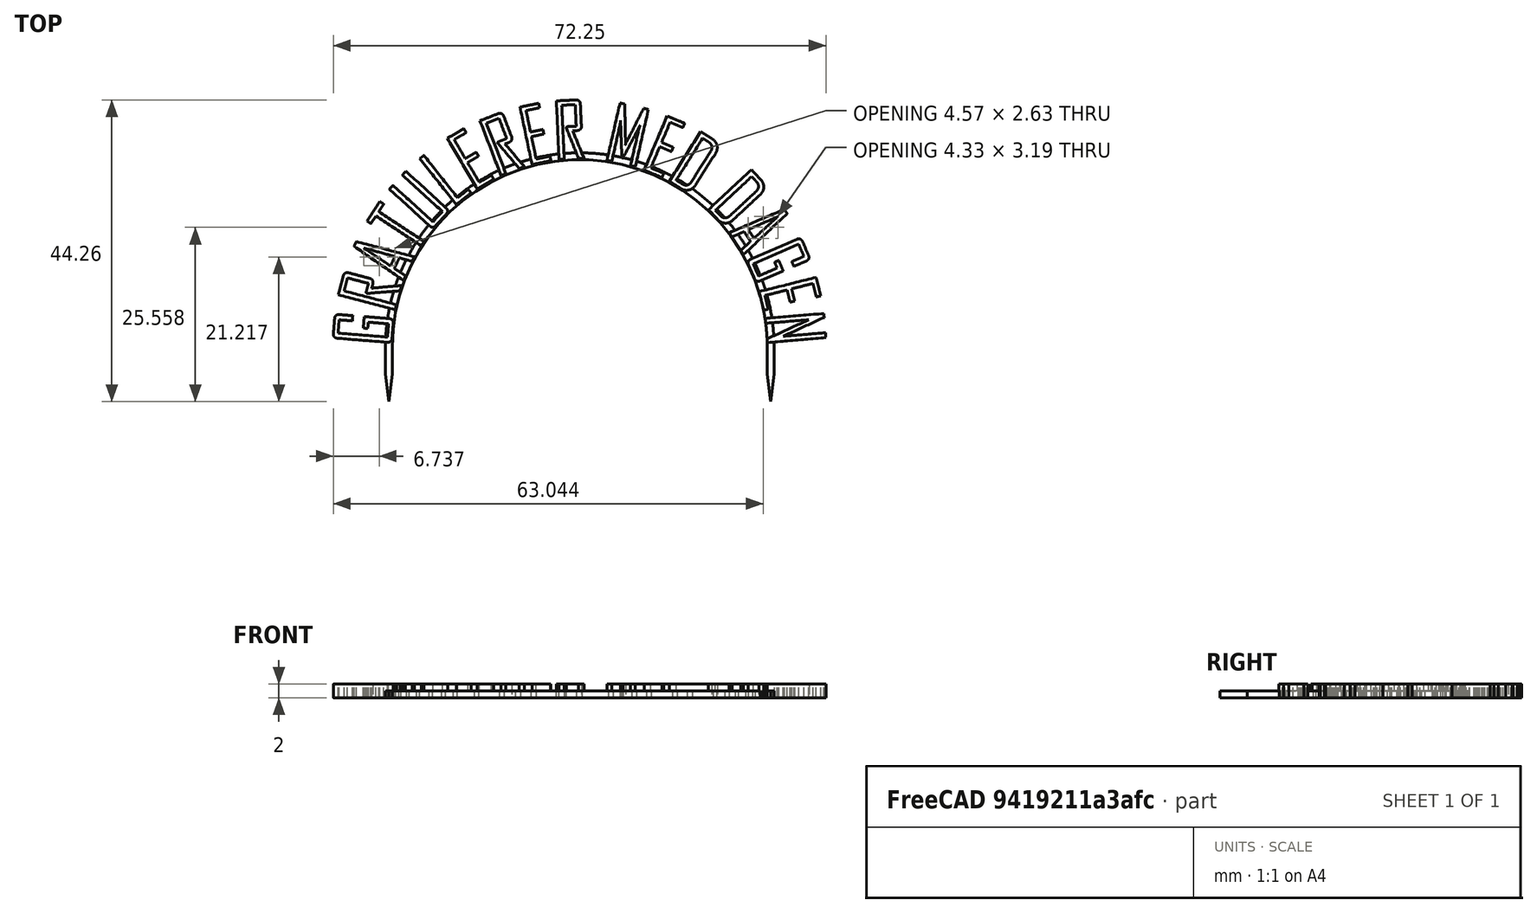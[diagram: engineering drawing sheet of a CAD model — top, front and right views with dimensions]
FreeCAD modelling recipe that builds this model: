
FCSTD DOCUMENT  (FreeCAD 0.20R29177 (Git))
Label: cake-topper-gratulerer-med-dagen-caps
License: All rights reserved
LicenseURL: http://en.wikipedia.org/wiki/All_rights_reserved
objects: Part::Feature×22, Sketcher::SketchObject×4, PartDesign::Pad×4, App::DocumentObjectGroup×3, App::TextDocument×1, Spreadsheet::Sheet×1, PartDesign::Plane×1, PartDesign::Body×1, Mesh::Feature×1
note: 36 computed .brp shape members not serialized (recipe doc carries the construction recipe); baked Part::Feature solids carry a one-line shape summary decoded from their .brp

FEATURE [App::TextDocument] Text_document  label="Text document"
FEATURE [Spreadsheet::Sheet] Spreadsheet
  cells = A1=Text height; B1=text_h; C1(dim_text_h)==2mm; A2=Text offset x; B2=text_x; C2(dim_text_x)==-105.3mm; A3=Text offset y; B3=text_y; C3(dim_text_y)==177.4mm; A4=Scaffold height; B4=scaffold_h; C4(dim_scaffold_h)==1mm; A5=Scaffold width; B5=scaffold_w; C5(dim_scaffold_w)==1mm; A6=Scaffold inner radius; B6=scaffold_ir; C6(dim_scaffold_ir)==27.5mm; A7=Scaffold outer radius; B7=scaffold_or; C7(dim_scaffold_or)==dim_scaffold_ir + dim_scaffold_w; A8=Tines length; B8=tine_l; C8(dim_tine_l)==4mm; A9=Tines shaft length; B9=tine_shaft_l; C9(dim_tine_shaft_l)==4mm
FEATURE [PartDesign::Plane] DatumPlane  label="BaseXYDatumPlane"
  Length = 85.5553
  MapMode = 5
  ResizeMode = 0
  Support = -> [XY_Plane]
  Width = 74.5697
FEATURE [Sketcher::SketchObject] Sketch001  label="ArcSketch"
  FullyConstrained = true
  MapMode = 5
  Support = -> [DatumPlane]
  expr: Constraints[15] = Spreadsheet.dim_scaffold_or
  expr: Constraints[38] = Spreadsheet.dim_tine_shaft_l
  expr: Constraints[39] = Spreadsheet.dim_tine_l
  expr: Constraints[65] = Spreadsheet.dim_scaffold_or
  expr: Constraints[6] = Spreadsheet.dim_scaffold_ir
  sketch-geometry (26):
    g0: ArcOfCircle CenterX=0 CenterY=0 CenterZ=0 NormalX=0 NormalY=0 NormalZ=1 AngleXU=0 Radius=27.5 StartAngle=0 EndAngle=3.14159
    g1: LineSegment StartX=-28.5 StartY=3.5e-15 StartZ=0 EndX=-27.5 EndY=3.4e-15 EndZ=0
    g2: LineSegment StartX=27.5 StartY=0 StartZ=0 EndX=28.5 EndY=0 EndZ=0
    g3: ArcOfCircle CenterX=0 CenterY=0 CenterZ=0 NormalX=0 NormalY=0 NormalZ=1 AngleXU=0 Radius=28.5 StartAngle=1.44096 EndAngle=3.14159
    g4: ArcOfCircle CenterX=0 CenterY=0 CenterZ=0 NormalX=0 NormalY=0 NormalZ=1 AngleXU=0 Radius=28.5 StartAngle=0 EndAngle=1.40587
    g5: ArcOfCircle CenterX=0 CenterY=0 CenterZ=0 NormalX=0 NormalY=0 NormalZ=1 AngleXU=0 Radius=28.5 StartAngle=1.40587 EndAngle=1.44096
    g6: LineSegment StartX=3.69 StartY=28.2601 StartZ=0 EndX=5.12878 EndY=38.3822 EndZ=0
    g7: LineSegment StartX=4.67918 StartY=28.1133 StartZ=0 EndX=6.11883 EndY=38.2415 EndZ=0
    g8: LineSegment StartX=5.12878 StartY=38.3822 StartZ=0 EndX=6.11883 EndY=38.2415 EndZ=0
    g9: LineSegment StartX=-28.5 StartY=3.5e-15 StartZ=0 EndX=-28.5 EndY=-4 EndZ=0
    g10: LineSegment StartX=-27.5 StartY=3.4e-15 StartZ=0 EndX=-27.5 EndY=-4 EndZ=0
    g11: LineSegment StartX=-28.5 StartY=-4 StartZ=0 EndX=-28 EndY=-8 EndZ=0
    g12: LineSegment StartX=-27.5 StartY=-4 StartZ=0 EndX=-28 EndY=-8 EndZ=0
    g13: LineSegment StartX=-28.5 StartY=-4 StartZ=0 EndX=-28 EndY=-4 EndZ=0
    g14: LineSegment StartX=-28 StartY=-4 StartZ=0 EndX=-27.5 EndY=-4 EndZ=0
    g15: LineSegment StartX=-28 StartY=-4 StartZ=0 EndX=-28 EndY=-8 EndZ=0
    g16: LineSegment StartX=27.5 StartY=-4 StartZ=0 EndX=28 EndY=-4 EndZ=0
    g17: LineSegment StartX=28 StartY=-4 StartZ=0 EndX=28.5 EndY=-4 EndZ=0
    g18: LineSegment StartX=28 StartY=-4 StartZ=0 EndX=28 EndY=-8 EndZ=0
    g19: LineSegment StartX=27.5 StartY=0 StartZ=0 EndX=27.5 EndY=-4 EndZ=0
    g20: LineSegment StartX=28.5 StartY=0 StartZ=0 EndX=28.5 EndY=-4 EndZ=0
    g21: LineSegment StartX=27.5 StartY=-4 StartZ=0 EndX=28 EndY=-8 EndZ=0
    g22: LineSegment StartX=28.5 StartY=-4 StartZ=0 EndX=28 EndY=-8 EndZ=0
    g23: LineSegment StartX=3.69 StartY=28.2601 StartZ=0 EndX=0 EndY=28.2601 EndZ=0
    g24: LineSegment StartX=28.5 StartY=0 StartZ=0 EndX=28.5 EndY=28.5 EndZ=0
    g25: LineSegment StartX=28.5 StartY=28.5 StartZ=0 EndX=4.73415 EndY=28.5 EndZ=0
  constraints (71):
    c: Coincident(g0,g-1)
    c: PointOnObject(g0,g-1)
    c: PointOnObject(g0,g-1)
    c: Coincident(g4,g0)
    c: PointOnObject(g3,g-1)
    c: PointOnObject(g4,g-1)
    c: Radius(g0) = 27.5
    c: Coincident(g1,g3)
    c: Coincident(g1,g0)
    c: Coincident(g2,g0)
    c: Coincident(g2,g4)
    c: Coincident(g5,g3)
    c: Coincident(g4,g3)
    c: Coincident(g4,g5)
    c: Coincident(g4,g5)
    c: Radius(g4) = 28.5
    c: Coincident(g6,g3)
    c: Coincident(g7,g4)
    c: Coincident(g8,g6)
    c: Coincident(g8,g7)
    c: Parallel(g6,g7)
    c: Perpendicular(g8,g6)
    c: Coincident(g9,g3)
    c: Vertical(g9)
    c: Coincident(g10,g0)
    c: Vertical(g10)
    c: Coincident(g11,g9)
    c: Coincident(g12,g10)
    c: Coincident(g12,g11)
    c: Coincident(g13,g9)
    c: Horizontal(g13)
    c: Coincident(g14,g13)
    c: Coincident(g14,g10)
    c: Horizontal(g14)
    c: Coincident(g15,g13)
    c: Coincident(g15,g11)
    c: Equal(g14,g13)
    c: Vertical(g15)
    c: DistanceY(g10,g10) = 4
    c: DistanceY(g11,g10) = 4
    c: Horizontal(g16)
    c: Coincident(g17,g16)
    c: Horizontal(g17)
    c: Coincident(g18,g16)
    c: Vertical(g18)
    c: Coincident(g19,g0)
    c: Coincident(g19,g16)
    c: Vertical(g19)
    c: Coincident(g20,g4)
    c: Coincident(g20,g17)
    c: Vertical(g20)
    c: Coincident(g21,g19)
    c: Coincident(g21,g18)
    c: Coincident(g22,g20)
    c: Coincident(g22,g21)
    c: Equal(g19,g10)
    c: Equal(g18,g15)
    c: Equal(g17,g16)
    c: Distance(g8) = 1
    c: Coincident(g23,g3)
    c: PointOnObject(g23,g-2)
    c: Horizontal(g23)
    c: DistanceX(g23,g23) = 3.69
    c: Coincident(g24,g4)
    c: Vertical(g24)
    c: DistanceY(g24,g24) = 28.5
    c: Coincident(g25,g24)
    c: PointOnObject(g25,g7)
    c: Horizontal(g25)
    c: Angle(g25,g7) = 1.4296
    c: Distance(g7) = 10.23
FEATURE [PartDesign::Pad] Pad  label="ArcPad"
  Direction = (0,0,1)
  Length = 1
  Length2 = 10
  Profile = -> Sketch001
  ReferenceAxis = -> Sketch001 [N_Axis]
  Type = 0
  expr: Length = Spreadsheet.dim_scaffold_h
FEATURE [Part::Feature] path26706
  shape: bbox 8.818 x 4.113 x 2e-07 mm, 0 faces, 0 solids (baked)
FEATURE [Part::Feature] path26708
  shape: bbox 9.277 x 5.465 x 2e-07 mm, 0 faces, 0 solids (baked)
FEATURE [Part::Feature] path26710
  shape: bbox 8.816 x 5.676 x 2e-07 mm, 0 faces, 0 solids (baked)
FEATURE [Part::Feature] path26710001
  shape: bbox 4.566 x 2.632 x 2e-07 mm, 0 faces, 0 solids (baked)
FEATURE [Part::Feature] path26712
  shape: bbox 8.371 x 6.488 x 2e-07 mm, 0 faces, 0 solids (baked)
FEATURE [Part::Feature] path26714
  shape: bbox 8.547 x 8.23 x 2e-07 mm, 0 faces, 0 solids (baked)
FEATURE [Part::Feature] path26716
  shape: bbox 7.527 x 7.228 x 2e-07 mm, 0 faces, 0 solids (baked)
FEATURE [Part::Feature] path26718
  shape: bbox 6.804 x 8.859 x 2e-07 mm, 0 faces, 0 solids (baked)
FEATURE [Part::Feature] path26720
  shape: bbox 6.53 x 9.155 x 2e-07 mm, 0 faces, 0 solids (baked)
FEATURE [Part::Feature] path26722
  shape: bbox 4.54 x 9.017 x 2e-07 mm, 0 faces, 0 solids (baked)
FEATURE [Part::Feature] path26724
  shape: bbox 4.063 x 8.762 x 2e-07 mm, 0 faces, 0 solids (baked)
FEATURE [App::DocumentObjectGroup] Group  label="GratulererGroup"
  Group = -> [path26706,path26708,path26710,path26710001,path26712,path26714,path26716,path26718,path26720,path26722,path26724]
FEATURE [Part::Feature] path26726
  shape: bbox 6.071 x 9.357 x 2e-07 mm, 0 faces, 0 solids (baked)
FEATURE [Part::Feature] path26728
  shape: bbox 5.942 x 9.049 x 2e-07 mm, 0 faces, 0 solids (baked)
FEATURE [Part::Feature] path26730
  shape: bbox 7.088 x 8.663 x 2e-07 mm, 0 faces, 0 solids (baked)
FEATURE [Part::Feature] path26730001
  shape: bbox 5.278 x 6.906 x 2e-07 mm, 0 faces, 0 solids (baked)
FEATURE [App::DocumentObjectGroup] Group001  label="medGroup"
  Group = -> [path26726,path26728,path26730,path26730001]
FEATURE [Part::Feature] path26732
  shape: bbox 8.126 x 7.885 x 2e-07 mm, 0 faces, 0 solids (baked)
FEATURE [Part::Feature] path26732001
  shape: bbox 6.334 x 6.087 x 2e-07 mm, 0 faces, 0 solids (baked)
FEATURE [Part::Feature] path26734
  shape: bbox 8.492 x 6.647 x 2e-07 mm, 0 faces, 0 solids (baked)
FEATURE [Part::Feature] path26734001
  shape: bbox 4.328 x 3.192 x 2e-07 mm, 0 faces, 0 solids (baked)
FEATURE [Part::Feature] path26736
  shape: bbox 8.97 x 6.298 x 2e-07 mm, 0 faces, 0 solids (baked)
FEATURE [Part::Feature] path26738
  shape: bbox 9.049 x 4.849 x 2e-07 mm, 0 faces, 0 solids (baked)
FEATURE [Part::Feature] path26740
  shape: bbox 8.892 x 4.259 x 2e-07 mm, 0 faces, 0 solids (baked)
FEATURE [App::DocumentObjectGroup] Group002  label="dagenGroup"
  Group = -> [path26732,path26732001,path26734,path26734001,path26736,path26738,path26740]
FEATURE [Sketcher::SketchObject] Sketch  label="GratulererSketch"
  FullyConstrained = false
  Placement = pos=(-105.3,177.4,0) rot=(0,0,1;0rad)
  expr: .Placement.Base.x = Spreadsheet.dim_text_x
  expr: .Placement.Base.y = Spreadsheet.dim_text_y
  sketch-geometry (138):
    g0: BSplineCurve PolesCount=3 KnotsCount=2 Degree=2 IsPeriodic=0
    g1: BSplineCurve PolesCount=3 KnotsCount=2 Degree=2 IsPeriodic=0
    g2: BSplineCurve PolesCount=2 KnotsCount=2 Degree=1 IsPeriodic=0
    g3: BSplineCurve PolesCount=3 KnotsCount=2 Degree=2 IsPeriodic=0
    g4: BSplineCurve PolesCount=3 KnotsCount=2 Degree=2 IsPeriodic=0
    g5: BSplineCurve PolesCount=2 KnotsCount=2 Degree=1 IsPeriodic=0
    g6: BSplineCurve PolesCount=3 KnotsCount=2 Degree=2 IsPeriodic=0
    g7: BSplineCurve PolesCount=3 KnotsCount=2 Degree=2 IsPeriodic=0
    g8: BSplineCurve PolesCount=2 KnotsCount=2 Degree=1 IsPeriodic=0
    g9: BSplineCurve PolesCount=3 KnotsCount=2 Degree=2 IsPeriodic=0
    g10: BSplineCurve PolesCount=3 KnotsCount=2 Degree=2 IsPeriodic=0
    g11: BSplineCurve PolesCount=2 KnotsCount=2 Degree=1 IsPeriodic=0
    g12: BSplineCurve PolesCount=2 KnotsCount=2 Degree=1 IsPeriodic=0
    g13: BSplineCurve PolesCount=2 KnotsCount=2 Degree=1 IsPeriodic=0
    g14: BSplineCurve PolesCount=2 KnotsCount=2 Degree=1 IsPeriodic=0
    g15: BSplineCurve PolesCount=2 KnotsCount=2 Degree=1 IsPeriodic=0
    g16: BSplineCurve PolesCount=2 KnotsCount=2 Degree=1 IsPeriodic=0
    g17: BSplineCurve PolesCount=2 KnotsCount=2 Degree=1 IsPeriodic=0
    g18: BSplineCurve PolesCount=2 KnotsCount=2 Degree=1 IsPeriodic=0
    g19: BSplineCurve PolesCount=2 KnotsCount=2 Degree=1 IsPeriodic=0
    g20: BSplineCurve PolesCount=2 KnotsCount=2 Degree=1 IsPeriodic=0
    g21: BSplineCurve PolesCount=2 KnotsCount=2 Degree=1 IsPeriodic=0
    g22: BSplineCurve PolesCount=2 KnotsCount=2 Degree=1 IsPeriodic=0
    g23: BSplineCurve PolesCount=2 KnotsCount=2 Degree=1 IsPeriodic=0
    g24: BSplineCurve PolesCount=2 KnotsCount=2 Degree=1 IsPeriodic=0
    g25: BSplineCurve PolesCount=2 KnotsCount=2 Degree=1 IsPeriodic=0
    g26: BSplineCurve PolesCount=2 KnotsCount=2 Degree=1 IsPeriodic=0
    g27: BSplineCurve PolesCount=2 KnotsCount=2 Degree=1 IsPeriodic=0
    g28: BSplineCurve PolesCount=2 KnotsCount=2 Degree=1 IsPeriodic=0
    g29: BSplineCurve PolesCount=2 KnotsCount=2 Degree=1 IsPeriodic=0
    g30: BSplineCurve PolesCount=2 KnotsCount=2 Degree=1 IsPeriodic=0
    g31: BSplineCurve PolesCount=2 KnotsCount=2 Degree=1 IsPeriodic=0
    g32: BSplineCurve PolesCount=3 KnotsCount=2 Degree=2 IsPeriodic=0
    g33: BSplineCurve PolesCount=3 KnotsCount=2 Degree=2 IsPeriodic=0
    g34: BSplineCurve PolesCount=2 KnotsCount=2 Degree=1 IsPeriodic=0
    g35: BSplineCurve PolesCount=3 KnotsCount=2 Degree=2 IsPeriodic=0
    g36: BSplineCurve PolesCount=3 KnotsCount=2 Degree=2 IsPeriodic=0
    g37: BSplineCurve PolesCount=3 KnotsCount=2 Degree=2 IsPeriodic=0
    g38: BSplineCurve PolesCount=3 KnotsCount=2 Degree=2 IsPeriodic=0
    g39: BSplineCurve PolesCount=2 KnotsCount=2 Degree=1 IsPeriodic=0
    g40: BSplineCurve PolesCount=2 KnotsCount=2 Degree=1 IsPeriodic=0
    g41: BSplineCurve PolesCount=2 KnotsCount=2 Degree=1 IsPeriodic=0
    g42: BSplineCurve PolesCount=2 KnotsCount=2 Degree=1 IsPeriodic=0
    g43: BSplineCurve PolesCount=2 KnotsCount=2 Degree=1 IsPeriodic=0
    g44: BSplineCurve PolesCount=2 KnotsCount=2 Degree=1 IsPeriodic=0
    g45: BSplineCurve PolesCount=2 KnotsCount=2 Degree=1 IsPeriodic=0
    g46: BSplineCurve PolesCount=2 KnotsCount=2 Degree=1 IsPeriodic=0
    g47: BSplineCurve PolesCount=2 KnotsCount=2 Degree=1 IsPeriodic=0
    g48: BSplineCurve PolesCount=2 KnotsCount=2 Degree=1 IsPeriodic=0
    g49: BSplineCurve PolesCount=2 KnotsCount=2 Degree=1 IsPeriodic=0
    g50: BSplineCurve PolesCount=2 KnotsCount=2 Degree=1 IsPeriodic=0
    g51: BSplineCurve PolesCount=2 KnotsCount=2 Degree=1 IsPeriodic=0
    g52: BSplineCurve PolesCount=2 KnotsCount=2 Degree=1 IsPeriodic=0
    g53: BSplineCurve PolesCount=2 KnotsCount=2 Degree=1 IsPeriodic=0
    g54: BSplineCurve PolesCount=2 KnotsCount=2 Degree=1 IsPeriodic=0
    g55: BSplineCurve PolesCount=2 KnotsCount=2 Degree=1 IsPeriodic=0
    g56: BSplineCurve PolesCount=2 KnotsCount=2 Degree=1 IsPeriodic=0
    g57: BSplineCurve PolesCount=2 KnotsCount=2 Degree=1 IsPeriodic=0
    g58: BSplineCurve PolesCount=2 KnotsCount=2 Degree=1 IsPeriodic=0
    g59: BSplineCurve PolesCount=2 KnotsCount=2 Degree=1 IsPeriodic=0
    g60: BSplineCurve PolesCount=3 KnotsCount=2 Degree=2 IsPeriodic=0
    g61: BSplineCurve PolesCount=3 KnotsCount=2 Degree=2 IsPeriodic=0
    g62: BSplineCurve PolesCount=2 KnotsCount=2 Degree=1 IsPeriodic=0
    g63: BSplineCurve PolesCount=3 KnotsCount=2 Degree=2 IsPeriodic=0
    g64: BSplineCurve PolesCount=3 KnotsCount=2 Degree=2 IsPeriodic=0
    g65: BSplineCurve PolesCount=2 KnotsCount=2 Degree=1 IsPeriodic=0
    g66: BSplineCurve PolesCount=2 KnotsCount=2 Degree=1 IsPeriodic=0
    g67: BSplineCurve PolesCount=2 KnotsCount=2 Degree=1 IsPeriodic=0
    g68: BSplineCurve PolesCount=2 KnotsCount=2 Degree=1 IsPeriodic=0
    g69: BSplineCurve PolesCount=2 KnotsCount=2 Degree=1 IsPeriodic=0
    g70: BSplineCurve PolesCount=2 KnotsCount=2 Degree=1 IsPeriodic=0
    g71: BSplineCurve PolesCount=2 KnotsCount=2 Degree=1 IsPeriodic=0
    g72: BSplineCurve PolesCount=2 KnotsCount=2 Degree=1 IsPeriodic=0
    g73: BSplineCurve PolesCount=2 KnotsCount=2 Degree=1 IsPeriodic=0
    g74: BSplineCurve PolesCount=2 KnotsCount=2 Degree=1 IsPeriodic=0
    g75: BSplineCurve PolesCount=2 KnotsCount=2 Degree=1 IsPeriodic=0
    g76: BSplineCurve PolesCount=2 KnotsCount=2 Degree=1 IsPeriodic=0
    g77: BSplineCurve PolesCount=2 KnotsCount=2 Degree=1 IsPeriodic=0
    g78: BSplineCurve PolesCount=2 KnotsCount=2 Degree=1 IsPeriodic=0
    g79: BSplineCurve PolesCount=2 KnotsCount=2 Degree=1 IsPeriodic=0
    g80: BSplineCurve PolesCount=2 KnotsCount=2 Degree=1 IsPeriodic=0
    g81: BSplineCurve PolesCount=2 KnotsCount=2 Degree=1 IsPeriodic=0
    g82: BSplineCurve PolesCount=2 KnotsCount=2 Degree=1 IsPeriodic=0
    g83: BSplineCurve PolesCount=2 KnotsCount=2 Degree=1 IsPeriodic=0
    g84: BSplineCurve PolesCount=2 KnotsCount=2 Degree=1 IsPeriodic=0
    g85: BSplineCurve PolesCount=2 KnotsCount=2 Degree=1 IsPeriodic=0
    g86: BSplineCurve PolesCount=2 KnotsCount=2 Degree=1 IsPeriodic=0
    g87: BSplineCurve PolesCount=2 KnotsCount=2 Degree=1 IsPeriodic=0
    g88: BSplineCurve PolesCount=2 KnotsCount=2 Degree=1 IsPeriodic=0
    g89: BSplineCurve PolesCount=2 KnotsCount=2 Degree=1 IsPeriodic=0
    g90: BSplineCurve PolesCount=2 KnotsCount=2 Degree=1 IsPeriodic=0
    g91: BSplineCurve PolesCount=2 KnotsCount=2 Degree=1 IsPeriodic=0
    g92: BSplineCurve PolesCount=2 KnotsCount=2 Degree=1 IsPeriodic=0
    g93: BSplineCurve PolesCount=2 KnotsCount=2 Degree=1 IsPeriodic=0
    g94: BSplineCurve PolesCount=2 KnotsCount=2 Degree=1 IsPeriodic=0
    g95: BSplineCurve PolesCount=2 KnotsCount=2 Degree=1 IsPeriodic=0
    g96: BSplineCurve PolesCount=2 KnotsCount=2 Degree=1 IsPeriodic=0
    g97: BSplineCurve PolesCount=2 KnotsCount=2 Degree=1 IsPeriodic=0
    g98: BSplineCurve PolesCount=2 KnotsCount=2 Degree=1 IsPeriodic=0
    g99: BSplineCurve PolesCount=2 KnotsCount=2 Degree=1 IsPeriodic=0
    g100: BSplineCurve PolesCount=3 KnotsCount=2 Degree=2 IsPeriodic=0
    g101: BSplineCurve PolesCount=3 KnotsCount=2 Degree=2 IsPeriodic=0
    g102: BSplineCurve PolesCount=2 KnotsCount=2 Degree=1 IsPeriodic=0
    g103: BSplineCurve PolesCount=3 KnotsCount=2 Degree=2 IsPeriodic=0
    g104: BSplineCurve PolesCount=3 KnotsCount=2 Degree=2 IsPeriodic=0
    g105: BSplineCurve PolesCount=3 KnotsCount=2 Degree=2 IsPeriodic=0
    g106: BSplineCurve PolesCount=3 KnotsCount=2 Degree=2 IsPeriodic=0
    g107: BSplineCurve PolesCount=2 KnotsCount=2 Degree=1 IsPeriodic=0
    g108: BSplineCurve PolesCount=2 KnotsCount=2 Degree=1 IsPeriodic=0
    g109: BSplineCurve PolesCount=2 KnotsCount=2 Degree=1 IsPeriodic=0
    g110: BSplineCurve PolesCount=2 KnotsCount=2 Degree=1 IsPeriodic=0
    g111: BSplineCurve PolesCount=2 KnotsCount=2 Degree=1 IsPeriodic=0
    g112: BSplineCurve PolesCount=2 KnotsCount=2 Degree=1 IsPeriodic=0
    g113: BSplineCurve PolesCount=2 KnotsCount=2 Degree=1 IsPeriodic=0
    g114: BSplineCurve PolesCount=2 KnotsCount=2 Degree=1 IsPeriodic=0
    g115: BSplineCurve PolesCount=2 KnotsCount=2 Degree=1 IsPeriodic=0
    g116: BSplineCurve PolesCount=2 KnotsCount=2 Degree=1 IsPeriodic=0
    g117: BSplineCurve PolesCount=2 KnotsCount=2 Degree=1 IsPeriodic=0
    g118: BSplineCurve PolesCount=2 KnotsCount=2 Degree=1 IsPeriodic=0
    g119: BSplineCurve PolesCount=2 KnotsCount=2 Degree=1 IsPeriodic=0
    g120: BSplineCurve PolesCount=2 KnotsCount=2 Degree=1 IsPeriodic=0
    g121: BSplineCurve PolesCount=2 KnotsCount=2 Degree=1 IsPeriodic=0
    g122: BSplineCurve PolesCount=2 KnotsCount=2 Degree=1 IsPeriodic=0
    g123: BSplineCurve PolesCount=2 KnotsCount=2 Degree=1 IsPeriodic=0
    g124: BSplineCurve PolesCount=2 KnotsCount=2 Degree=1 IsPeriodic=0
    g125: BSplineCurve PolesCount=2 KnotsCount=2 Degree=1 IsPeriodic=0
    g126: BSplineCurve PolesCount=2 KnotsCount=2 Degree=1 IsPeriodic=0
    g127: BSplineCurve PolesCount=2 KnotsCount=2 Degree=1 IsPeriodic=0
    g128: BSplineCurve PolesCount=2 KnotsCount=2 Degree=1 IsPeriodic=0
    g129: BSplineCurve PolesCount=2 KnotsCount=2 Degree=1 IsPeriodic=0
    g130: BSplineCurve PolesCount=3 KnotsCount=2 Degree=2 IsPeriodic=0
    g131: BSplineCurve PolesCount=3 KnotsCount=2 Degree=2 IsPeriodic=0
    g132: BSplineCurve PolesCount=2 KnotsCount=2 Degree=1 IsPeriodic=0
    g133: BSplineCurve PolesCount=3 KnotsCount=2 Degree=2 IsPeriodic=0
    g134: BSplineCurve PolesCount=3 KnotsCount=2 Degree=2 IsPeriodic=0
    g135: BSplineCurve PolesCount=3 KnotsCount=2 Degree=2 IsPeriodic=0
    g136: BSplineCurve PolesCount=3 KnotsCount=2 Degree=2 IsPeriodic=0
    g137: BSplineCurve PolesCount=2 KnotsCount=2 Degree=1 IsPeriodic=0
  constraints (138):
    c: Coincident(g0,g1)
    c: Coincident(g1,g2)
    c: Coincident(g2,g3)
    c: Coincident(g3,g4)
    c: Coincident(g4,g5)
    c: Coincident(g5,g6)
    c: Coincident(g6,g7)
    c: Coincident(g7,g8)
    c: Coincident(g8,g9)
    c: Coincident(g9,g10)
    c: Coincident(g10,g11)
    c: Coincident(g11,g12)
    c: Coincident(g12,g13)
    c: Coincident(g13,g14)
    c: Coincident(g14,g15)
    c: Coincident(g15,g16)
    c: Coincident(g16,g17)
    c: Coincident(g17,g18)
    c: Coincident(g18,g19)
    c: Coincident(g19,g20)
    c: Coincident(g20,g21)
    c: Coincident(g21,g0)
    c: Coincident(g22,g23)
    c: Coincident(g23,g24)
    c: Coincident(g24,g25)
    c: Coincident(g25,g26)
    c: Coincident(g26,g27)
    c: Coincident(g27,g28)
    c: Coincident(g28,g29)
    c: Coincident(g29,g30)
    c: Coincident(g30,g31)
    c: Coincident(g31,g32)
    c: Coincident(g32,g33)
    c: Coincident(g33,g34)
    c: Coincident(g34,g35)
    c: Coincident(g35,g36)
    c: Coincident(g36,g37)
    c: Coincident(g37,g38)
    c: Coincident(g38,g39)
    c: Coincident(g39,g22)
    c: Coincident(g40,g41)
    c: Coincident(g41,g42)
    c: Coincident(g42,g43)
    c: Coincident(g43,g44)
    c: Coincident(g44,g45)
    c: Coincident(g45,g46)
    c: Coincident(g46,g47)
    c: Coincident(g47,g48)
    c: Coincident(g48,g40)
    c: Coincident(g49,g50)
    c: Coincident(g50,g51)
    c: Coincident(g51,g49)
    c: Coincident(g52,g53)
    c: Coincident(g53,g54)
    c: Coincident(g54,g55)
    c: Coincident(g55,g56)
    c: Coincident(g56,g57)
    c: Coincident(g57,g58)
    c: Coincident(g58,g59)
    c: Coincident(g59,g52)
    c: Coincident(g60,g61)
    c: Coincident(g61,g62)
    c: Coincident(g62,g63)
    c: Coincident(g63,g64)
    c: Coincident(g64,g65)
    c: Coincident(g65,g66)
    c: Coincident(g66,g67)
    c: Coincident(g67,g68)
    c: Coincident(g68,g69)
    c: Coincident(g69,g70)
    c: Coincident(g70,g71)
    c: Coincident(g71,g60)
    c: Coincident(g72,g73)
    c: Coincident(g73,g74)
    c: Coincident(g74,g75)
    c: Coincident(g75,g76)
    c: Coincident(g76,g77)
    c: Coincident(g77,g72)
    c: Coincident(g78,g79)
    c: Coincident(g79,g80)
    c: Coincident(g80,g81)
    c: Coincident(g81,g82)
    c: Coincident(g82,g83)
    c: Coincident(g83,g84)
    c: Coincident(g84,g85)
    c: Coincident(g85,g86)
    c: Coincident(g86,g87)
    c: Coincident(g87,g88)
    c: Coincident(g88,g89)
    c: Coincident(g89,g78)
    c: Coincident(g90,g91)
    c: Coincident(g91,g92)
    c: Coincident(g92,g93)
    c: Coincident(g93,g94)
    c: Coincident(g94,g95)
    c: Coincident(g95,g96)
    c: Coincident(g96,g97)
    c: Coincident(g97,g98)
    c: Coincident(g98,g99)
    c: Coincident(g99,g100)
    c: Coincident(g100,g101)
    c: Coincident(g101,g102)
    c: Coincident(g102,g103)
    c: Coincident(g103,g104)
    c: Coincident(g104,g105)
    c: Coincident(g105,g106)
    c: Coincident(g106,g107)
    c: Coincident(g107,g90)
    c: Coincident(g108,g109)
    c: Coincident(g109,g110)
    c: Coincident(g110,g111)
    c: Coincident(g111,g112)
    c: Coincident(g112,g113)
    c: Coincident(g113,g114)
    c: Coincident(g114,g115)
    c: Coincident(g115,g116)
    c: Coincident(g116,g117)
    c: Coincident(g117,g118)
    c: Coincident(g118,g119)
    c: Coincident(g119,g108)
    c: Coincident(g120,g121)
    c: Coincident(g121,g122)
    c: Coincident(g122,g123)
    c: Coincident(g123,g124)
    c: Coincident(g124,g125)
    c: Coincident(g125,g126)
    c: Coincident(g126,g127)
    c: Coincident(g127,g128)
    c: Coincident(g128,g129)
    c: Coincident(g129,g130)
    c: Coincident(g130,g131)
    c: Coincident(g131,g132)
    c: Coincident(g132,g133)
    c: Coincident(g133,g134)
    c: Coincident(g134,g135)
    c: Coincident(g135,g136)
    c: Coincident(g136,g137)
    c: Coincident(g137,g120)
FEATURE [Sketcher::SketchObject] Sketch002  label="MedSketch"
  FullyConstrained = false
  Placement = pos=(-105.3,177.4,0) rot=(0,0,1;0rad)
  expr: .Placement.Base.x = Spreadsheet.dim_text_x
  expr: .Placement.Base.y = Spreadsheet.dim_text_y
  sketch-geometry (45):
    g0: BSplineCurve PolesCount=2 KnotsCount=2 Degree=1 IsPeriodic=0
    g1: BSplineCurve PolesCount=2 KnotsCount=2 Degree=1 IsPeriodic=0
    g2: BSplineCurve PolesCount=3 KnotsCount=2 Degree=2 IsPeriodic=0
    g3: BSplineCurve PolesCount=2 KnotsCount=2 Degree=1 IsPeriodic=0
    g4: BSplineCurve PolesCount=2 KnotsCount=2 Degree=1 IsPeriodic=0
    g5: BSplineCurve PolesCount=2 KnotsCount=2 Degree=1 IsPeriodic=0
    g6: BSplineCurve PolesCount=3 KnotsCount=2 Degree=2 IsPeriodic=0
    g7: BSplineCurve PolesCount=2 KnotsCount=2 Degree=1 IsPeriodic=0
    g8: BSplineCurve PolesCount=2 KnotsCount=2 Degree=1 IsPeriodic=0
    g9: BSplineCurve PolesCount=2 KnotsCount=2 Degree=1 IsPeriodic=0
    g10: BSplineCurve PolesCount=2 KnotsCount=2 Degree=1 IsPeriodic=0
    g11: BSplineCurve PolesCount=2 KnotsCount=2 Degree=1 IsPeriodic=0
    g12: BSplineCurve PolesCount=3 KnotsCount=2 Degree=2 IsPeriodic=0
    g13: BSplineCurve PolesCount=3 KnotsCount=2 Degree=2 IsPeriodic=0
    g14: BSplineCurve PolesCount=2 KnotsCount=2 Degree=1 IsPeriodic=0
    g15: BSplineCurve PolesCount=2 KnotsCount=2 Degree=1 IsPeriodic=0
    g16: BSplineCurve PolesCount=2 KnotsCount=2 Degree=1 IsPeriodic=0
    g17: BSplineCurve PolesCount=2 KnotsCount=2 Degree=1 IsPeriodic=0
    g18: BSplineCurve PolesCount=2 KnotsCount=2 Degree=1 IsPeriodic=0
    g19: BSplineCurve PolesCount=2 KnotsCount=2 Degree=1 IsPeriodic=0
    g20: BSplineCurve PolesCount=2 KnotsCount=2 Degree=1 IsPeriodic=0
    g21: BSplineCurve PolesCount=2 KnotsCount=2 Degree=1 IsPeriodic=0
    g22: BSplineCurve PolesCount=2 KnotsCount=2 Degree=1 IsPeriodic=0
    g23: BSplineCurve PolesCount=2 KnotsCount=2 Degree=1 IsPeriodic=0
    g24: BSplineCurve PolesCount=2 KnotsCount=2 Degree=1 IsPeriodic=0
    g25: BSplineCurve PolesCount=2 KnotsCount=2 Degree=1 IsPeriodic=0
    g26: BSplineCurve PolesCount=2 KnotsCount=2 Degree=1 IsPeriodic=0
    g27: BSplineCurve PolesCount=2 KnotsCount=2 Degree=1 IsPeriodic=0
    g28: BSplineCurve PolesCount=2 KnotsCount=2 Degree=1 IsPeriodic=0
    g29: BSplineCurve PolesCount=3 KnotsCount=2 Degree=2 IsPeriodic=0
    g30: BSplineCurve PolesCount=3 KnotsCount=2 Degree=2 IsPeriodic=0
    g31: BSplineCurve PolesCount=2 KnotsCount=2 Degree=1 IsPeriodic=0
    g32: BSplineCurve PolesCount=2 KnotsCount=2 Degree=1 IsPeriodic=0
    g33: BSplineCurve PolesCount=2 KnotsCount=2 Degree=1 IsPeriodic=0
    g34: BSplineCurve PolesCount=3 KnotsCount=2 Degree=2 IsPeriodic=0
    g35: BSplineCurve PolesCount=3 KnotsCount=2 Degree=2 IsPeriodic=0
    g36: BSplineCurve PolesCount=2 KnotsCount=2 Degree=1 IsPeriodic=0
    g37: BSplineCurve PolesCount=2 KnotsCount=2 Degree=1 IsPeriodic=0
    g38: BSplineCurve PolesCount=3 KnotsCount=2 Degree=2 IsPeriodic=0
    g39: BSplineCurve PolesCount=3 KnotsCount=2 Degree=2 IsPeriodic=0
    g40: BSplineCurve PolesCount=2 KnotsCount=2 Degree=1 IsPeriodic=0
    g41: BSplineCurve PolesCount=2 KnotsCount=2 Degree=1 IsPeriodic=0
    g42: BSplineCurve PolesCount=2 KnotsCount=2 Degree=1 IsPeriodic=0
    g43: BSplineCurve PolesCount=3 KnotsCount=2 Degree=2 IsPeriodic=0
    g44: BSplineCurve PolesCount=3 KnotsCount=2 Degree=2 IsPeriodic=0
  constraints (45):
    c: Coincident(g0,g1)
    c: Coincident(g1,g2)
    c: Coincident(g2,g3)
    c: Coincident(g3,g4)
    c: Coincident(g4,g5)
    c: Coincident(g5,g6)
    c: Coincident(g6,g7)
    c: Coincident(g7,g8)
    c: Coincident(g8,g9)
    c: Coincident(g9,g10)
    c: Coincident(g10,g11)
    c: Coincident(g11,g12)
    c: Coincident(g12,g13)
    c: Coincident(g13,g14)
    c: Coincident(g14,g15)
    c: Coincident(g15,g16)
    c: Coincident(g16,g0)
    c: Coincident(g17,g18)
    c: Coincident(g18,g19)
    c: Coincident(g19,g20)
    c: Coincident(g20,g21)
    c: Coincident(g21,g22)
    c: Coincident(g22,g23)
    c: Coincident(g23,g24)
    c: Coincident(g24,g25)
    c: Coincident(g25,g26)
    c: Coincident(g26,g27)
    c: Coincident(g27,g28)
    c: Coincident(g28,g17)
    c: Coincident(g29,g30)
    c: Coincident(g30,g31)
    c: Coincident(g31,g32)
    c: Coincident(g32,g33)
    c: Coincident(g33,g34)
    c: Coincident(g34,g35)
    c: Coincident(g35,g36)
    c: Coincident(g36,g29)
    c: Coincident(g37,g38)
    c: Coincident(g38,g39)
    c: Coincident(g39,g40)
    c: Coincident(g40,g41)
    c: Coincident(g41,g42)
    c: Coincident(g42,g43)
    c: Coincident(g43,g44)
    c: Coincident(g44,g37)
FEATURE [Sketcher::SketchObject] Sketch003  label="DagenSketch"
  FullyConstrained = false
  Placement = pos=(-105.3,177.4,0) rot=(0,0,1;0rad)
  expr: .Placement.Base.x = Spreadsheet.dim_text_x
  expr: .Placement.Base.y = Spreadsheet.dim_text_y
  sketch-geometry (72):
    g0: BSplineCurve PolesCount=3 KnotsCount=2 Degree=2 IsPeriodic=0
    g1: BSplineCurve PolesCount=3 KnotsCount=2 Degree=2 IsPeriodic=0
    g2: BSplineCurve PolesCount=2 KnotsCount=2 Degree=1 IsPeriodic=0
    g3: BSplineCurve PolesCount=2 KnotsCount=2 Degree=1 IsPeriodic=0
    g4: BSplineCurve PolesCount=2 KnotsCount=2 Degree=1 IsPeriodic=0
    g5: BSplineCurve PolesCount=3 KnotsCount=2 Degree=2 IsPeriodic=0
    g6: BSplineCurve PolesCount=3 KnotsCount=2 Degree=2 IsPeriodic=0
    g7: BSplineCurve PolesCount=2 KnotsCount=2 Degree=1 IsPeriodic=0
    g8: BSplineCurve PolesCount=2 KnotsCount=2 Degree=1 IsPeriodic=0
    g9: BSplineCurve PolesCount=3 KnotsCount=2 Degree=2 IsPeriodic=0
    g10: BSplineCurve PolesCount=3 KnotsCount=2 Degree=2 IsPeriodic=0
    g11: BSplineCurve PolesCount=2 KnotsCount=2 Degree=1 IsPeriodic=0
    g12: BSplineCurve PolesCount=2 KnotsCount=2 Degree=1 IsPeriodic=0
    g13: BSplineCurve PolesCount=2 KnotsCount=2 Degree=1 IsPeriodic=0
    g14: BSplineCurve PolesCount=3 KnotsCount=2 Degree=2 IsPeriodic=0
    g15: BSplineCurve PolesCount=3 KnotsCount=2 Degree=2 IsPeriodic=0
    g16: BSplineCurve PolesCount=2 KnotsCount=2 Degree=1 IsPeriodic=0
    g17: BSplineCurve PolesCount=2 KnotsCount=2 Degree=1 IsPeriodic=0
    g18: BSplineCurve PolesCount=2 KnotsCount=2 Degree=1 IsPeriodic=0
    g19: BSplineCurve PolesCount=2 KnotsCount=2 Degree=1 IsPeriodic=0
    g20: BSplineCurve PolesCount=2 KnotsCount=2 Degree=1 IsPeriodic=0
    g21: BSplineCurve PolesCount=2 KnotsCount=2 Degree=1 IsPeriodic=0
    g22: BSplineCurve PolesCount=2 KnotsCount=2 Degree=1 IsPeriodic=0
    g23: BSplineCurve PolesCount=2 KnotsCount=2 Degree=1 IsPeriodic=0
    g24: BSplineCurve PolesCount=2 KnotsCount=2 Degree=1 IsPeriodic=0
    g25: BSplineCurve PolesCount=2 KnotsCount=2 Degree=1 IsPeriodic=0
    g26: BSplineCurve PolesCount=2 KnotsCount=2 Degree=1 IsPeriodic=0
    g27: BSplineCurve PolesCount=2 KnotsCount=2 Degree=1 IsPeriodic=0
    g28: BSplineCurve PolesCount=3 KnotsCount=2 Degree=2 IsPeriodic=0
    g29: BSplineCurve PolesCount=3 KnotsCount=2 Degree=2 IsPeriodic=0
    g30: BSplineCurve PolesCount=2 KnotsCount=2 Degree=1 IsPeriodic=0
    g31: BSplineCurve PolesCount=3 KnotsCount=2 Degree=2 IsPeriodic=0
    g32: BSplineCurve PolesCount=3 KnotsCount=2 Degree=2 IsPeriodic=0
    g33: BSplineCurve PolesCount=2 KnotsCount=2 Degree=1 IsPeriodic=0
    g34: BSplineCurve PolesCount=3 KnotsCount=2 Degree=2 IsPeriodic=0
    g35: BSplineCurve PolesCount=3 KnotsCount=2 Degree=2 IsPeriodic=0
    g36: BSplineCurve PolesCount=2 KnotsCount=2 Degree=1 IsPeriodic=0
    g37: BSplineCurve PolesCount=3 KnotsCount=2 Degree=2 IsPeriodic=0
    g38: BSplineCurve PolesCount=3 KnotsCount=2 Degree=2 IsPeriodic=0
    g39: BSplineCurve PolesCount=2 KnotsCount=2 Degree=1 IsPeriodic=0
    g40: BSplineCurve PolesCount=2 KnotsCount=2 Degree=1 IsPeriodic=0
    g41: BSplineCurve PolesCount=2 KnotsCount=2 Degree=1 IsPeriodic=0
    g42: BSplineCurve PolesCount=2 KnotsCount=2 Degree=1 IsPeriodic=0
    g43: BSplineCurve PolesCount=2 KnotsCount=2 Degree=1 IsPeriodic=0
    g44: BSplineCurve PolesCount=2 KnotsCount=2 Degree=1 IsPeriodic=0
    g45: BSplineCurve PolesCount=2 KnotsCount=2 Degree=1 IsPeriodic=0
    g46: BSplineCurve PolesCount=2 KnotsCount=2 Degree=1 IsPeriodic=0
    g47: BSplineCurve PolesCount=2 KnotsCount=2 Degree=1 IsPeriodic=0
    g48: BSplineCurve PolesCount=2 KnotsCount=2 Degree=1 IsPeriodic=0
    g49: BSplineCurve PolesCount=2 KnotsCount=2 Degree=1 IsPeriodic=0
    g50: BSplineCurve PolesCount=2 KnotsCount=2 Degree=1 IsPeriodic=0
    g51: BSplineCurve PolesCount=2 KnotsCount=2 Degree=1 IsPeriodic=0
    g52: BSplineCurve PolesCount=2 KnotsCount=2 Degree=1 IsPeriodic=0
    g53: BSplineCurve PolesCount=2 KnotsCount=2 Degree=1 IsPeriodic=0
    g54: BSplineCurve PolesCount=2 KnotsCount=2 Degree=1 IsPeriodic=0
    g55: BSplineCurve PolesCount=2 KnotsCount=2 Degree=1 IsPeriodic=0
    g56: BSplineCurve PolesCount=2 KnotsCount=2 Degree=1 IsPeriodic=0
    g57: BSplineCurve PolesCount=2 KnotsCount=2 Degree=1 IsPeriodic=0
    g58: BSplineCurve PolesCount=2 KnotsCount=2 Degree=1 IsPeriodic=0
    g59: BSplineCurve PolesCount=2 KnotsCount=2 Degree=1 IsPeriodic=0
    g60: BSplineCurve PolesCount=2 KnotsCount=2 Degree=1 IsPeriodic=0
    g61: BSplineCurve PolesCount=2 KnotsCount=2 Degree=1 IsPeriodic=0
    g62: BSplineCurve PolesCount=2 KnotsCount=2 Degree=1 IsPeriodic=0
    g63: BSplineCurve PolesCount=2 KnotsCount=2 Degree=1 IsPeriodic=0
    g64: BSplineCurve PolesCount=2 KnotsCount=2 Degree=1 IsPeriodic=0
    g65: BSplineCurve PolesCount=2 KnotsCount=2 Degree=1 IsPeriodic=0
    g66: BSplineCurve PolesCount=2 KnotsCount=2 Degree=1 IsPeriodic=0
    g67: BSplineCurve PolesCount=2 KnotsCount=2 Degree=1 IsPeriodic=0
    g68: BSplineCurve PolesCount=2 KnotsCount=2 Degree=1 IsPeriodic=0
    g69: BSplineCurve PolesCount=2 KnotsCount=2 Degree=1 IsPeriodic=0
    g70: BSplineCurve PolesCount=2 KnotsCount=2 Degree=1 IsPeriodic=0
    g71: BSplineCurve PolesCount=2 KnotsCount=2 Degree=1 IsPeriodic=0
  constraints (72):
    c: Coincident(g0,g1)
    c: Coincident(g1,g2)
    c: Coincident(g2,g3)
    c: Coincident(g3,g4)
    c: Coincident(g4,g5)
    c: Coincident(g5,g6)
    c: Coincident(g6,g7)
    c: Coincident(g7,g0)
    c: Coincident(g8,g9)
    c: Coincident(g9,g10)
    c: Coincident(g10,g11)
    c: Coincident(g11,g12)
    c: Coincident(g12,g13)
    c: Coincident(g13,g14)
    c: Coincident(g14,g15)
    c: Coincident(g15,g8)
    c: Coincident(g16,g17)
    c: Coincident(g17,g18)
    c: Coincident(g18,g19)
    c: Coincident(g19,g20)
    c: Coincident(g20,g21)
    c: Coincident(g21,g22)
    c: Coincident(g22,g23)
    c: Coincident(g23,g24)
    c: Coincident(g24,g16)
    c: Coincident(g25,g26)
    c: Coincident(g26,g27)
    c: Coincident(g27,g25)
    c: Coincident(g28,g29)
    c: Coincident(g29,g30)
    c: Coincident(g30,g31)
    c: Coincident(g31,g32)
    c: Coincident(g32,g33)
    c: Coincident(g33,g34)
    c: Coincident(g34,g35)
    c: Coincident(g35,g36)
    c: Coincident(g36,g37)
    c: Coincident(g37,g38)
    c: Coincident(g38,g39)
    c: Coincident(g39,g40)
    c: Coincident(g40,g41)
    c: Coincident(g41,g42)
    c: Coincident(g42,g43)
    c: Coincident(g43,g44)
    c: Coincident(g44,g45)
    c: Coincident(g45,g46)
    c: Coincident(g46,g47)
    c: Coincident(g47,g48)
    c: Coincident(g48,g49)
    c: Coincident(g49,g28)
    c: Coincident(g50,g51)
    c: Coincident(g51,g52)
    c: Coincident(g52,g53)
    c: Coincident(g53,g54)
    c: Coincident(g54,g55)
    c: Coincident(g55,g56)
    c: Coincident(g56,g57)
    c: Coincident(g57,g58)
    c: Coincident(g58,g59)
    c: Coincident(g59,g60)
    c: Coincident(g60,g61)
    c: Coincident(g61,g50)
    c: Coincident(g62,g63)
    c: Coincident(g63,g64)
    c: Coincident(g64,g65)
    c: Coincident(g65,g66)
    c: Coincident(g66,g67)
    c: Coincident(g67,g68)
    c: Coincident(g68,g69)
    c: Coincident(g69,g70)
    c: Coincident(g70,g71)
    c: Coincident(g71,g62)
FEATURE [PartDesign::Pad] Pad001  label="GratulererPad"
  BaseFeature = -> Pad
  Direction = (0,0,1)
  Length = 2
  Length2 = 10
  Profile = -> Sketch
  ReferenceAxis = -> Sketch [N_Axis]
  Type = 0
  expr: Length = Spreadsheet.dim_text_h
FEATURE [PartDesign::Pad] Pad002  label="MedPad"
  BaseFeature = -> Pad001
  Direction = (0,0,1)
  Length = 2
  Length2 = 10
  Profile = -> Sketch002
  ReferenceAxis = -> Sketch002 [N_Axis]
  Type = 0
  expr: Length = Spreadsheet.dim_text_h
FEATURE [PartDesign::Pad] Pad003  label="DagenPad"
  BaseFeature = -> Pad002
  Direction = (0,0,1)
  Length = 2
  Length2 = 10
  Profile = -> Sketch003
  ReferenceAxis = -> Sketch003 [N_Axis]
  Type = 0
  expr: Length = Spreadsheet.dim_text_h
FEATURE [PartDesign::Body] Body
  Group = -> [DatumPlane,Sketch001,Pad,Sketch,Sketch002,Sketch003,Pad001,Pad002,Pad003]
  Origin = -> Origin
  Tip = -> Pad003
FEATURE [Mesh::Feature] Mesh  label="Body (Meshed)"
